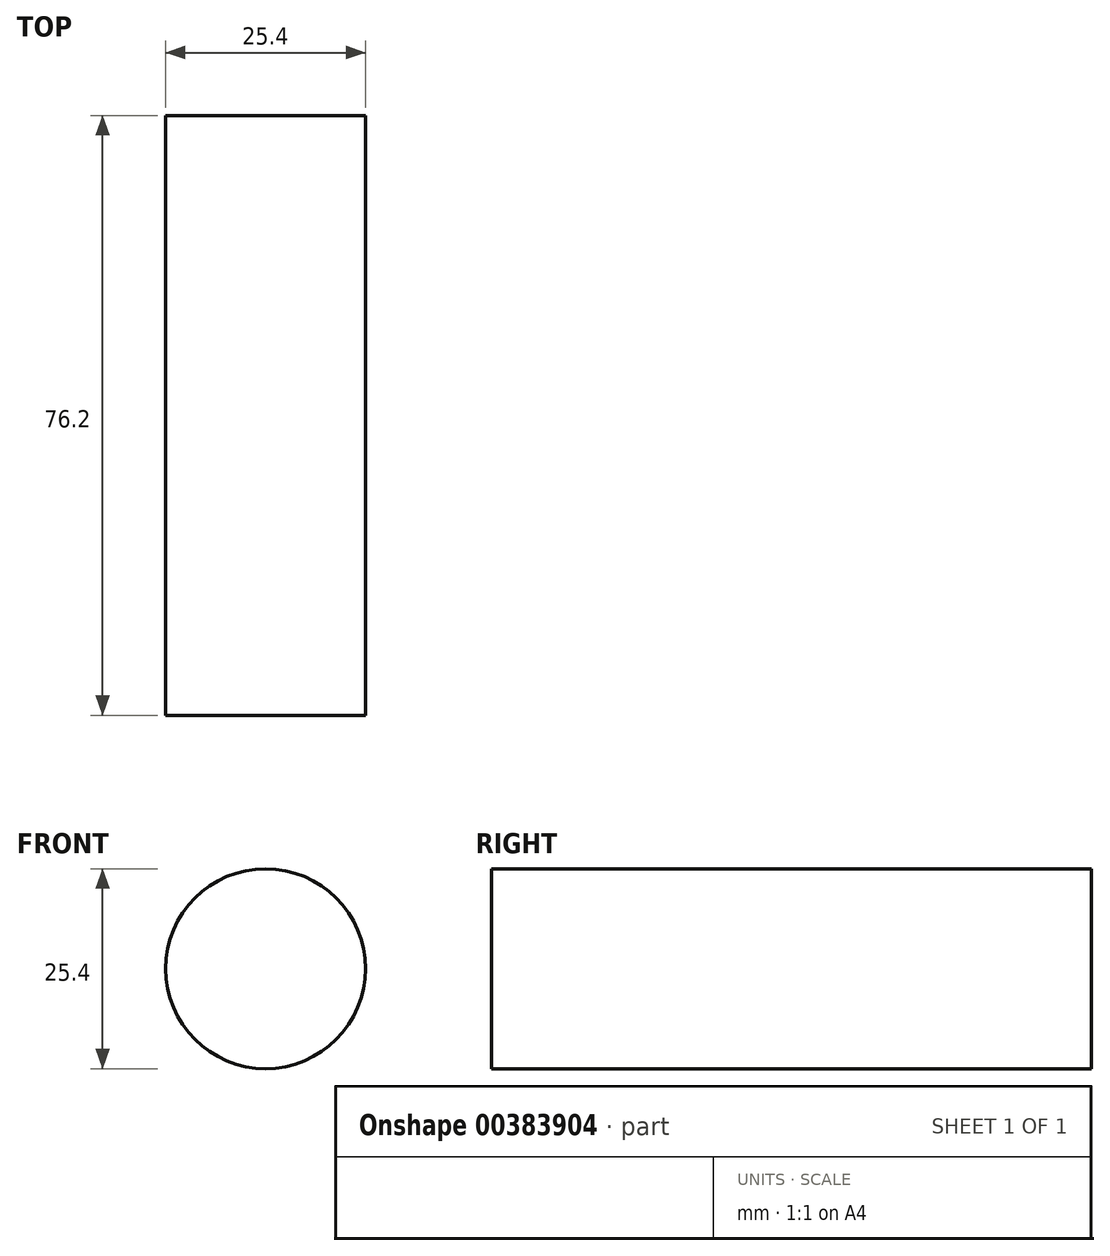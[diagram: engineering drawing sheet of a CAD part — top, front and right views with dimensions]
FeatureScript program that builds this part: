
annotation { "Feature Type Name" : "Feature", "Feature Type Description" : "" }
export const myFeature = defineFeature(function(context is Context, id is Id, definition is map)
    precondition{}
    {
        {
            var Q0;
            Q0=qCreatedBy(makeId("Front.planeOp"),FACE);
            var sketch = newSketch(context, id + "F0", { "sketchPlane" : qUnion([Q0])});
            skCircle(sketch, "E0", {"center": v(0, 0) * mm, "radius": 12.7 * mm});
            skSolve(sketch);
        }
        {
            var Q0;
            Q0=makeQuery(id+"F0.imprint","IMPRINT",FACE,{"disambiguationData":[TD([[makeQuery(id+"F0.imprint","IMPRINT",EDGE,{"derivedFrom":sQuery(id+"F0.wireOp",EDGE,"E0")}),1.0]])]});
            var Q1;
            Q1=sQuery(id+"F0.wireOp",EDGE,"E0");
            extrude(context, id + "F1", {"entities" : qUnion([Q0]), "surfaceEntities" : qUnion([Q1]), "depth" : 76.2 * mm});
        }
    });
